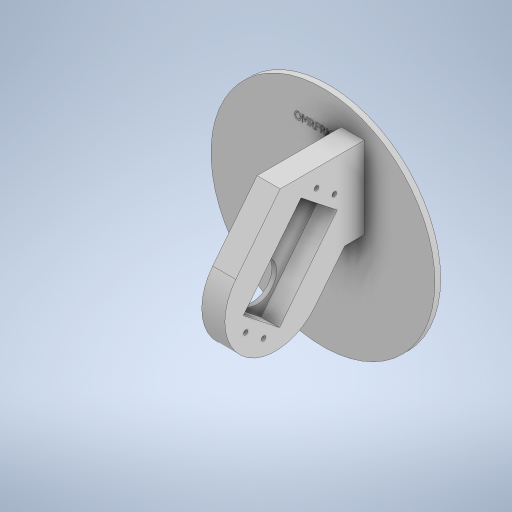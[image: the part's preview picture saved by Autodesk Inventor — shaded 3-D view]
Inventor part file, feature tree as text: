
AUTODESK INVENTOR PART (.ipt)
format: ipt  version: 2023.2 (Build 272271000, 271)  size: 468,480 bytes
history: native  units: mm
features: sketch x8, extrude x3, hole x3, emboss x1, plane x1
ambient origin geometry x8: Origin, YZ Plane, XZ Plane, XY Plane, X Axis, Y Axis, Z Axis, Center Point
bodies: Solid1 (feature_tree)
feature tree (16):
  extrude  "Extrusion1"  Depth=2.5mm TaperAngle=0.0deg
  hole  "Hole1"  [1 undecoded]
  hole  "Hole2"  [1 undecoded]
  emboss  "Emboss1"
  plane  "Work Plane1"
  extrude  "Extrusion2"  Depth=40.3mm
  extrude  "Extrusion3"  Depth=54.0mm
  hole  "Hole3"  [1 undecoded]
  sketch  "Sketch8"  dims[d26=2.5mm d27=2.5mm d28=10.0mm d29=0.0mm d30=19.9mm d31=40.3mm d32=9.85mm d33=17.0mm d34=54.0mm d35=2.5mm d36=2.5mm d37=8.0mm d38=0.0mm d39=49.422mm d40=9.85mm d41=2.0mm d42=6.0mm d43=4.0mm d44=2.0mm d45=90.0deg d46=7.0mm d47=0.0mm d48=15.419mm d49=35.158mm d50=35.158mm d51=9.85mm d52=15.419mm d54=9.85mm]
  sketch  "Sketch1"  dims[d0=97.0mm d1=2.5mm d2=0.0mm]
  sketch  "Sketch2"  dims[d3=15.0mm]
  sketch  "Sketch3"  dims[d4=2.1mm d5=6.0mm d6=4.0mm d7=2.0mm d8=90.0deg d9=8.0mm d10=0.0mm]
  sketch  "Sketch4"  dims[d11=8.0mm d12=6.0mm d13=4.0mm d14=2.0mm d15=90.0deg d16=8.0mm d17=0.0mm d18=1.0mm d19=0.0mm]
  sketch  "Sketch5"  dims[d20=8.0mm d21=19.9mm]
  sketch  "Sketch6"  dims[d22=40.3mm d23=9.85mm]
  sketch  "Sketch7"  dims[d24=17.0mm d25=54.0mm]
note: 3 required parameter values undecoded (feature->parameter linkage not recoverable at this tier; creation-order binding heuristic only, values carry confidence <= 0.55)
